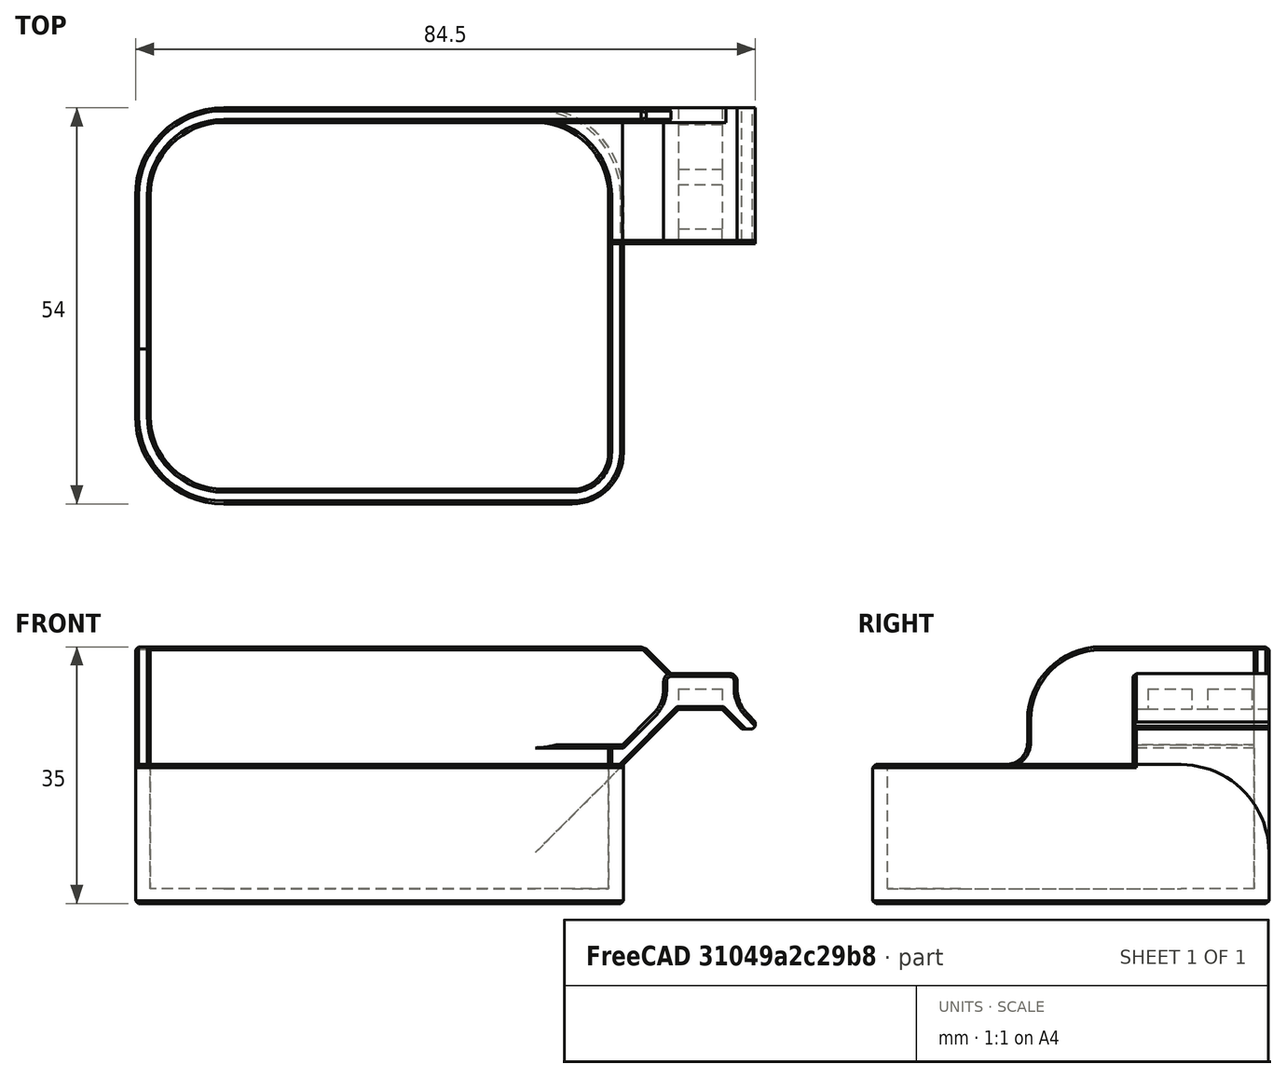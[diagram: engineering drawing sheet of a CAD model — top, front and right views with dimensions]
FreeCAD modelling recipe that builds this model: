
FCSTD DOCUMENT  (FreeCAD 0.19R24291 (Git))
Label: bucket-mod
License: Other
LicenseURL: GPL3
objects: Part::Cut×7, Part::Box×6, Part::Chamfer×4, Part::Feature×2, Part::Extrusion×1
note: 20 computed .brp shape members not serialized (recipe doc carries the construction recipe); baked Part::Feature solids carry a one-line shape summary decoded from their .brp

FEATURE [Part::Feature] Solid001001001  label="300mm002"
  Placement = pos=(-25.86,17,0) rot=(0,0,1;4.71239rad)
  shape: bbox 127 x 54 x 35 mm, 150 faces (baked)
FEATURE [Part::Box] Box  label="Cube"
  AttacherType = Attacher::AttachEngine3D
  Height = 59
  Length = 44
  Placement = pos=(0,-27.72,-3) rot=(0,0,1;0rad)
  Width = 76
FEATURE [Part::Cut] Cut
  Base = -> Solid001001001
  Tool = -> Box
FEATURE [Part::Box] Box001  label="Cube001"
  AttacherType = Attacher::AttachEngine3D
  Height = 7
  Length = 25
  Placement = pos=(-20.5,11.73,31.25) rot=(0,0,1;0rad)
  Width = 24
FEATURE [Part::Box] Box002  label="Cube002"
  AttacherType = Attacher::AttachEngine3D
  Height = 59
  Length = 10
  Placement = pos=(-4,-27.27,-13) rot=(0,0,1;0rad)
  Width = 61
FEATURE [Part::Cut] Cut001
  Base = -> Cut
  Tool = -> Box002
FEATURE [Part::Feature] Common_cs
  shape: bbox 8 x 3e-07 x 10.4 mm, 0 faces, 0 solids (baked)
FEATURE [Part::Extrusion] Extrude
  Base = -> Common_cs
  Dir = (0,1,0)
  DirMode = 2
  FaceMakerClass = Part::FaceMakerBullseye
  LengthFwd = 32
  LengthRev = 0
  Solid = true
  Symmetric = false
FEATURE [Part::Box] Box003  label="Cube003"
  AttacherType = Attacher::AttachEngine3D
  Height = 16
  Length = 10
  Placement = pos=(-9,14,22) rot=(0,0,1;0rad)
  Width = 28
FEATURE [Part::Chamfer] Chamfer
  Base = -> Box003
  Edges = 1 edges r=4: [Edge4]
FEATURE [Part::Cut] Cut002
  Base = -> Chamfer
  Tool = -> Extrude
FEATURE [Part::Cut] Cut003
  Base = -> Cut001
  Tool = -> Cut002
FEATURE [Part::Chamfer] Chamfer001
  Base = -> Box001
  Edges = 1 edges r=4: [Edge4]
FEATURE [Part::Cut] Cut004
  Base = -> Cut003
  Tool = -> Chamfer001
FEATURE [Part::Box] Box004  label="Cube004"
  AttacherType = Attacher::AttachEngine3D
  Height = 10
  Length = 10
  Placement = pos=(-10,10,13.68) rot=(0,0,1;0rad)
  Width = 24
FEATURE [Part::Cut] Cut005
  Base = -> Cut004
  Tool = -> Box004
FEATURE [Part::Box] Box005  label="Cube005"
  AttacherType = Attacher::AttachEngine3D
  Height = 10
  Length = 10
  Placement = pos=(-5,10,17.68) rot=(0,0,1;0rad)
  Width = 24
FEATURE [Part::Cut] Cut006
  Base = -> Cut005
  Tool = -> Box005
FEATURE [Part::Chamfer] Chamfer002
  Base = -> Cut006
  Edges = 1 edges r=0.4: [Edge88]
FEATURE [Part::Chamfer] Chamfer003
  Base = -> Chamfer002
  Edges = 5 edges r=0.4: [Edge9,Edge64,Edge69,Edge70,Edge71]
